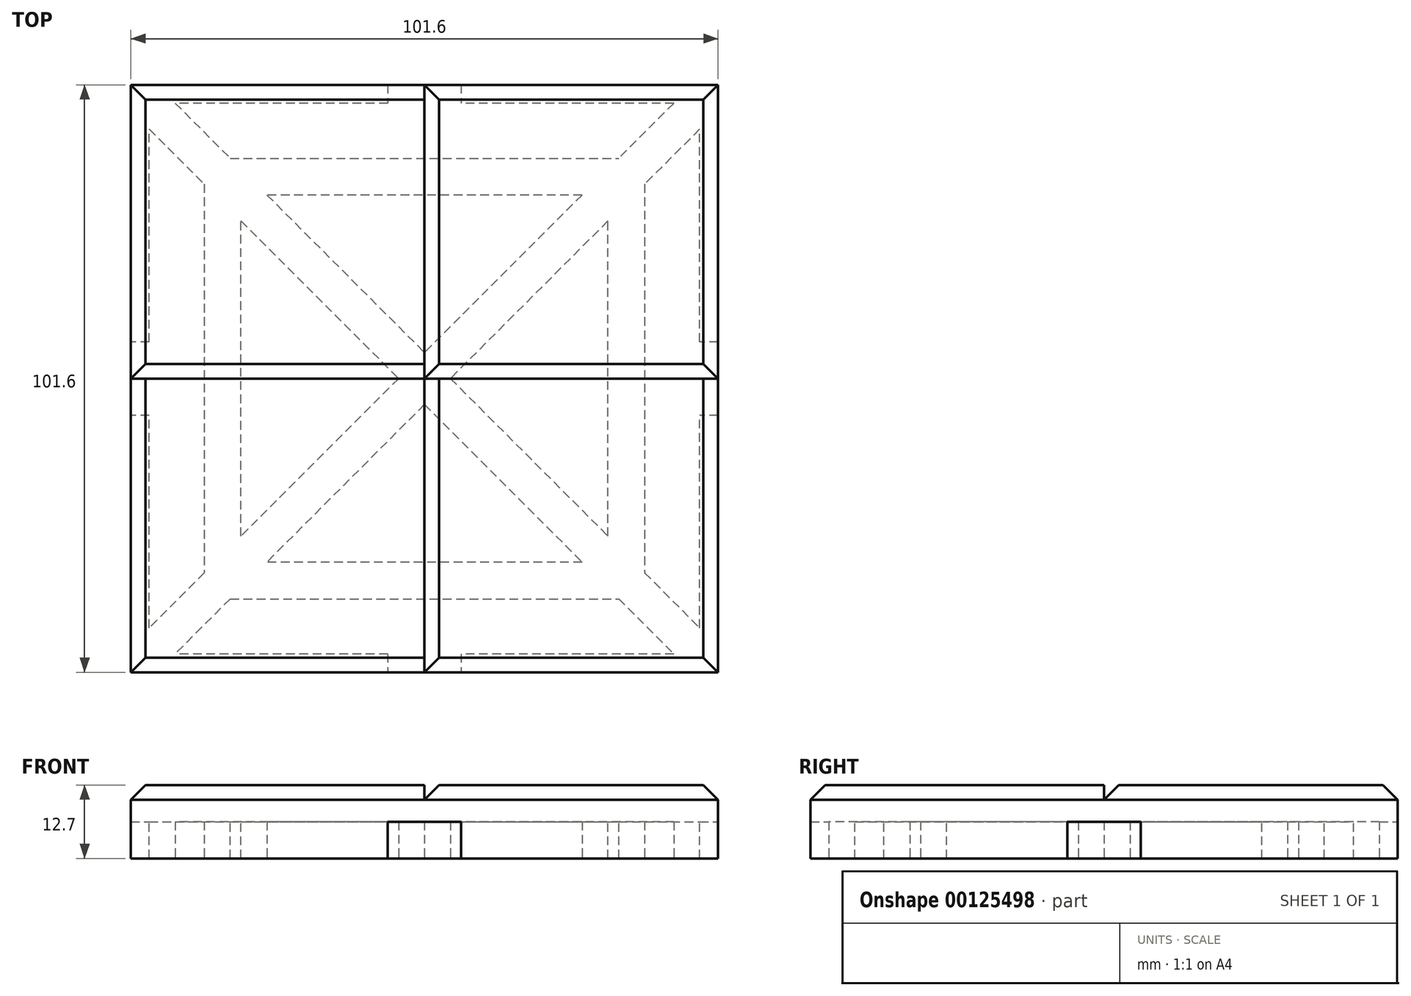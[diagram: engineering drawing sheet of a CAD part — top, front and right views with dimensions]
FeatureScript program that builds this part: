
annotation { "Feature Type Name" : "Feature", "Feature Type Description" : "" }
export const myFeature = defineFeature(function(context is Context, id is Id, definition is map)
    precondition{}
    {
        {
            var Q0;
            Q0=qCreatedBy(makeId("Top.planeOp"),FACE);
            var sketch = newSketch(context, id + "F0", { "sketchPlane" : qUnion([Q0])});
            skLineSegment(sketch, "E0.bottom", {"start": v(50.8, -50.8) * mm, "end": v(-50.8, -50.8) * mm});
            skLineSegment(sketch, "E0.top", {"start": v(50.8, 50.8) * mm, "end": v(-50.8, 50.8) * mm});
            skLineSegment(sketch, "E0.left", {"start": v(50.8, -50.8) * mm, "end": v(50.8, 50.8) * mm});
            skLineSegment(sketch, "E0.right", {"start": v(-50.8, -50.8) * mm, "end": v(-50.8, 50.8) * mm});
            skPoint(sketch, "E0.middle", {"position": v(0, 0) * mm});
            skLineSegment(sketch, "E1.bottom", {"start": v(47.63, -47.62) * mm, "end": v(-47.63, -47.63) * mm});
            skLineSegment(sketch, "E1.top", {"start": v(47.63, 47.63) * mm, "end": v(-47.63, 47.62) * mm});
            skLineSegment(sketch, "E1.left", {"start": v(47.63, -47.62) * mm, "end": v(47.63, 47.63) * mm});
            skLineSegment(sketch, "E1.right", {"start": v(-47.63, -47.63) * mm, "end": v(-47.63, 47.62) * mm});
            skSolve(sketch);
        }
        {
            var Q0;
            Q0=makeQuery(id+"F0.imprint","IMPRINT",FACE,{"disambiguationData":[TD([[makeQuery(id+"F0.imprint","IMPRINT",EDGE,{"derivedFrom":sQuery(id+"F0.wireOp",EDGE,"E0.bottom")}),-1.0]])]});
            var Q1;
            Q1=qNothing();
            var Q2;
            Q2=qNothing();
            extrude(context, id + "F1", {"entities" : qUnion([Q0]), "surfaceEntities" : qUnion([Q1, Q2]), "depth" : 6.35 * mm});
        }
        {
            var Q0;
            Q0=qCreatedBy(makeId("Top.planeOp"),FACE);
            var sketch = newSketch(context, id + "F2", { "sketchPlane" : qUnion([Q0])});
            skLineSegment(sketch, "E2.bottom", {"start": v(50.8, -6.35) * mm, "end": v(-50.8, -6.35) * mm});
            skLineSegment(sketch, "E2.top", {"start": v(50.8, 6.35) * mm, "end": v(-50.8, 6.35) * mm});
            skLineSegment(sketch, "E2.left", {"start": v(50.8, -6.35) * mm, "end": v(50.8, 6.35) * mm});
            skLineSegment(sketch, "E2.right", {"start": v(-50.8, -6.35) * mm, "end": v(-50.8, 6.35) * mm});
            skPoint(sketch, "E2.middle", {"position": v(0, 0) * mm});
            skLineSegment(sketch, "E3.bottom", {"start": v(6.35, 50.8) * mm, "end": v(-6.35, 50.8) * mm});
            skLineSegment(sketch, "E3.top", {"start": v(6.35, -50.8) * mm, "end": v(-6.35, -50.8) * mm});
            skLineSegment(sketch, "E3.left", {"start": v(6.35, 50.8) * mm, "end": v(6.35, -50.8) * mm});
            skLineSegment(sketch, "E3.right", {"start": v(-6.35, 50.8) * mm, "end": v(-6.35, -50.8) * mm});
            skLineSegment(sketch, "E4.bottom", {"start": v(-38.1, 38.1) * mm, "end": v(38.1, 38.1) * mm});
            skLineSegment(sketch, "E4.top", {"start": v(-38.1, -38.1) * mm, "end": v(38.1, -38.1) * mm});
            skLineSegment(sketch, "E4.left", {"start": v(-38.1, 38.1) * mm, "end": v(-38.1, -38.1) * mm});
            skLineSegment(sketch, "E4.right", {"start": v(38.1, 38.1) * mm, "end": v(38.1, -38.1) * mm});
            skLineSegment(sketch, "E5.bottom", {"start": v(31.75, -31.75) * mm, "end": v(-31.75, -31.75) * mm});
            skLineSegment(sketch, "E5.top", {"start": v(31.75, 31.75) * mm, "end": v(-31.75, 31.75) * mm});
            skLineSegment(sketch, "E5.left", {"start": v(31.75, -31.75) * mm, "end": v(31.75, 31.75) * mm});
            skLineSegment(sketch, "E5.right", {"start": v(-31.75, -31.75) * mm, "end": v(-31.75, 31.75) * mm});
            skSolve(sketch);
        }
        {
            var Q0;
            {var subQ0=sQuery(id+"F2.wireOp",EDGE,"E3.bottom");Q0=makeQuery(id+"F2.imprint","IMPRINT",FACE,{"disambiguationData":[TD([[makeQuery(id+"F2.imprint","IMPRINT",EDGE,{"derivedFrom":subQ0}),1.0]])]});}
            var Q1;
            {var subQ0=sQuery(id+"F2.wireOp",EDGE,"E2.left");Q1=makeQuery(id+"F2.imprint","IMPRINT",FACE,{"disambiguationData":[TD([[makeQuery(id+"F2.imprint","IMPRINT",EDGE,{"derivedFrom":subQ0}),1.0]])]});}
            var Q2;
            {var subQ0=sQuery(id+"F2.wireOp",EDGE,"E3.top");Q2=makeQuery(id+"F2.imprint","IMPRINT",FACE,{"disambiguationData":[TD([[makeQuery(id+"F2.imprint","IMPRINT",EDGE,{"derivedFrom":subQ0}),-1.0]])]});}
            var Q3;
            {var subQ0=sQuery(id+"F2.wireOp",EDGE,"E2.right");Q3=makeQuery(id+"F2.imprint","IMPRINT",FACE,{"disambiguationData":[TD([[makeQuery(id+"F2.imprint","IMPRINT",EDGE,{"derivedFrom":subQ0}),-1.0]])]});}
            extrude(context, id + "F3", {"entities" : qUnion([Q0, Q1, Q2, Q3]), "depth" : 25.4 * mm});
        }
        {
            var Q0;
            Q0=makeQuery(id+"F3.opExtrude","SWEPT_BODY",BODY,{"disambiguationData":[OSD([sQuery(id+"F2.wireOp",EDGE,"E3.bottom"),sQuery(id+"F2.wireOp",EDGE,"E3.left"),sQuery(id+"F2.wireOp",EDGE,"E3.right"),sQuery(id+"F2.wireOp",EDGE,"Qsms8eDc-lT19-7mVP-u5gy-GIsI6seksr0S")])]});
            var Q1;
            Q1=makeQuery(id+"F3.opExtrude","SWEPT_BODY",BODY,{"disambiguationData":[OSD([sQuery(id+"F2.wireOp",EDGE,"E2.bottom"),sQuery(id+"F2.wireOp",EDGE,"E2.top"),sQuery(id+"F2.wireOp",EDGE,"E2.left"),sQuery(id+"F2.wireOp",EDGE,"Qsms8eDc-lT19-7mVP-u5gy-GIsI6seksr0S")])]});
            var Q2;
            Q2=makeQuery(id+"F3.opExtrude","SWEPT_BODY",BODY,{"disambiguationData":[OSD([sQuery(id+"F2.wireOp",EDGE,"E3.top"),sQuery(id+"F2.wireOp",EDGE,"E3.left"),sQuery(id+"F2.wireOp",EDGE,"E3.right"),sQuery(id+"F2.wireOp",EDGE,"Qsms8eDc-lT19-7mVP-u5gy-GIsI6seksr0S")])]});
            var Q3;
            Q3=makeQuery(id+"F3.opExtrude","SWEPT_BODY",BODY,{"disambiguationData":[OSD([sQuery(id+"F2.wireOp",EDGE,"E2.bottom"),sQuery(id+"F2.wireOp",EDGE,"E2.top"),sQuery(id+"F2.wireOp",EDGE,"E2.right"),sQuery(id+"F2.wireOp",EDGE,"Qsms8eDc-lT19-7mVP-u5gy-GIsI6seksr0S")])]});
            var Q4;
            Q4=makeQuery(id+"F1.opExtrude","SWEPT_BODY",BODY,{"disambiguationData":[OSD([sQuery(id+"F0.wireOp",EDGE,"E0.bottom"),sQuery(id+"F0.wireOp",EDGE,"E0.top"),sQuery(id+"F0.wireOp",EDGE,"E0.left"),sQuery(id+"F0.wireOp",EDGE,"E0.right"),sQuery(id+"F0.wireOp",EDGE,"E1.bottom"),sQuery(id+"F0.wireOp",EDGE,"E1.top"),sQuery(id+"F0.wireOp",EDGE,"E1.left"),sQuery(id+"F0.wireOp",EDGE,"E1.right")])]});
            booleanBodies(context, id + "F4", {"operationType" : BooleanOperationType.SUBTRACTION, "tools" : qUnion([Q0, Q1, Q2, Q3]), "targets" : qUnion([Q4])});
        }
        {
            var Q0;
            {var subQ0=sQuery(id+"F2.wireOp",EDGE,"E4.left");var subQ3=sQuery(id+"F2.wireOp",EDGE,"E2.bottom");var subQ4=makeQuery(id+"F2.imprint","INTERSECT",VERTEX,{"derivedFrom":[subQ3,subQ0]});Q0=makeQuery(id+"F2.imprint","IMPRINT",FACE,{"disambiguationData":[TD([[makeQuery(id+"F2.imprint","IMPRINT",EDGE,{"disambiguationData":[TD([[subQ4,1.0]])],"derivedFrom":subQ3}),1.0]])]});}
            var Q1;
            {var subQ0=sQuery(id+"F2.wireOp",EDGE,"E4.top");var subQ1=sQuery(id+"F2.wireOp",EDGE,"E3.left");var subQ2=makeQuery(id+"F2.imprint","INTERSECT",VERTEX,{"derivedFrom":[subQ1,subQ0]});Q1=makeQuery(id+"F2.imprint","IMPRINT",FACE,{"disambiguationData":[TD([[makeQuery(id+"F2.imprint","IMPRINT",EDGE,{"disambiguationData":[TD([[subQ2,1.0]])],"derivedFrom":subQ1}),-1.0]])]});}
            var Q2;
            {var subQ0=sQuery(id+"F2.wireOp",EDGE,"E4.right");var subQ3=sQuery(id+"F2.wireOp",EDGE,"E2.bottom");var subQ4=makeQuery(id+"F2.imprint","INTERSECT",VERTEX,{"derivedFrom":[subQ3,subQ0]});Q2=makeQuery(id+"F2.imprint","IMPRINT",FACE,{"disambiguationData":[TD([[makeQuery(id+"F2.imprint","IMPRINT",EDGE,{"disambiguationData":[TD([[subQ4,-1.0]])],"derivedFrom":subQ3}),1.0]])]});}
            var Q3;
            {var subQ0=sQuery(id+"F2.wireOp",EDGE,"E4.right");var subQ1=sQuery(id+"F2.wireOp",EDGE,"E2.bottom");var subQ2=makeQuery(id+"F2.imprint","INTERSECT",VERTEX,{"derivedFrom":[subQ1,subQ0]});Q3=makeQuery(id+"F2.imprint","IMPRINT",FACE,{"disambiguationData":[TD([[makeQuery(id+"F2.imprint","IMPRINT",EDGE,{"disambiguationData":[TD([[subQ2,-1.0]])],"derivedFrom":subQ1}),-1.0]])]});}
            var Q4;
            {var subQ0=sQuery(id+"F2.wireOp",EDGE,"E4.right");var subQ7=sQuery(id+"F2.wireOp",EDGE,"E2.top");var subQ8=makeQuery(id+"F2.imprint","INTERSECT",VERTEX,{"derivedFrom":[subQ7,subQ0]});Q4=makeQuery(id+"F2.imprint","IMPRINT",FACE,{"disambiguationData":[TD([[makeQuery(id+"F2.imprint","IMPRINT",EDGE,{"disambiguationData":[TD([[subQ8,-1.0]])],"derivedFrom":subQ7}),-1.0]])]});}
            var Q5;
            {var subQ0=sQuery(id+"F2.wireOp",EDGE,"E4.bottom");var subQ1=sQuery(id+"F2.wireOp",EDGE,"E3.left");var subQ2=makeQuery(id+"F2.imprint","INTERSECT",VERTEX,{"derivedFrom":[subQ1,subQ0]});Q5=makeQuery(id+"F2.imprint","IMPRINT",FACE,{"disambiguationData":[TD([[makeQuery(id+"F2.imprint","IMPRINT",EDGE,{"disambiguationData":[TD([[subQ2,-1.0]])],"derivedFrom":subQ1}),-1.0]])]});}
            var Q6;
            {var subQ0=sQuery(id+"F2.wireOp",EDGE,"E4.left");var subQ3=sQuery(id+"F2.wireOp",EDGE,"E2.top");var subQ4=makeQuery(id+"F2.imprint","INTERSECT",VERTEX,{"derivedFrom":[subQ3,subQ0]});Q6=makeQuery(id+"F2.imprint","IMPRINT",FACE,{"disambiguationData":[TD([[makeQuery(id+"F2.imprint","IMPRINT",EDGE,{"disambiguationData":[TD([[subQ4,1.0]])],"derivedFrom":subQ3}),-1.0]])]});}
            var Q7;
            {var subQ0=sQuery(id+"F2.wireOp",EDGE,"E4.left");var subQ1=sQuery(id+"F2.wireOp",EDGE,"E2.bottom");var subQ2=makeQuery(id+"F2.imprint","INTERSECT",VERTEX,{"derivedFrom":[subQ1,subQ0]});Q7=makeQuery(id+"F2.imprint","IMPRINT",FACE,{"disambiguationData":[TD([[makeQuery(id+"F2.imprint","IMPRINT",EDGE,{"disambiguationData":[TD([[subQ2,1.0]])],"derivedFrom":subQ1}),-1.0]])]});}
            extrude(context, id + "F5", {"entities" : qUnion([Q0, Q1, Q2, Q3, Q4, Q5, Q6, Q7]), "depth" : 6.35 * mm});
        }
        {
            var Q0;
            Q0=qCreatedBy(makeId("Top.planeOp"),FACE);
            var sketch = newSketch(context, id + "F6", { "sketchPlane" : qUnion([Q0])});
            skLineSegment(sketch, "E6.bottom", {"start": v(3.18, 67.47) * mm, "end": v(-3.17, 67.47) * mm});
            skLineSegment(sketch, "E6.top", {"start": v(3.17, -67.47) * mm, "end": v(-3.18, -67.47) * mm});
            skLineSegment(sketch, "E6.left", {"start": v(3.18, 67.47) * mm, "end": v(3.17, -67.47) * mm});
            skLineSegment(sketch, "E6.right", {"start": v(-3.17, 67.47) * mm, "end": v(-3.18, -67.47) * mm});
            skPoint(sketch, "E6.middle", {"position": v(0, 0) * mm});
            skSolve(sketch);
        }
        {
            var Q0;
            Q0=makeQuery(id+"F6.imprint","IMPRINT",FACE,{"disambiguationData":[TD([[makeQuery(id+"F6.imprint","IMPRINT",EDGE,{"derivedFrom":sQuery(id+"F6.wireOp",EDGE,"E6.bottom")}),1.0]])]});
            extrude(context, id + "F7", {"entities" : qUnion([Q0]), "depth" : 6.35 * mm});
        }
        {
            var Q0;
            Q0=qCreatedBy(makeId("Front.planeOp"),FACE);
            var sketch = newSketch(context, id + "F8", { "sketchPlane" : qUnion([Q0])});
            skLineSegment(sketch, "E7", {"start": v(0, 0) * mm, "end": v(0, 25.4) * mm, "construction": true});
            skSolve(sketch);
        }
        {
            var Q0;
            Q0=makeQuery(id+"F7.opExtrude","SWEPT_BODY",BODY,{"disambiguationData":[OSD([sQuery(id+"F6.wireOp",EDGE,"E6.bottom"),sQuery(id+"F6.wireOp",EDGE,"E6.top"),sQuery(id+"F6.wireOp",EDGE,"E6.left"),sQuery(id+"F6.wireOp",EDGE,"E6.right")])]});
            var Q1;
            Q1=sQuery(id+"F8.wireOp",EDGE,"E7");
            transform(context, id + "F9", {"entities" : qUnion([Q0]), "transformType" : TransformType.ROTATION, "transformAxis" : qUnion([Q1]), "angle" : 45 * degree, "makeCopy" : true});
        }
        {
            var Q0;
            Q0=makeQuery(id+"F7.opExtrude","SWEPT_BODY",BODY,{"disambiguationData":[OSD([sQuery(id+"F6.wireOp",EDGE,"E6.bottom"),sQuery(id+"F6.wireOp",EDGE,"E6.top"),sQuery(id+"F6.wireOp",EDGE,"E6.left"),sQuery(id+"F6.wireOp",EDGE,"E6.right")])]});
            var Q1;
            Q1=sQuery(id+"F8.wireOp",EDGE,"E7");
            transform(context, id + "F10", {"entities" : qUnion([Q0]), "transformType" : TransformType.ROTATION, "transformAxis" : qUnion([Q1]), "angle" : 45 * degree, "oppositeDirection" : true, "makeCopy" : false});
        }
        {
            var Q0;
            Q0=makeQuery(id+"F9.opPattern","COPY",BODY,{"derivedFrom":makeQuery(id+"F7.opExtrude","SWEPT_BODY",BODY,{"disambiguationData":[OSD([sQuery(id+"F6.wireOp",EDGE,"E6.bottom"),sQuery(id+"F6.wireOp",EDGE,"E6.top"),sQuery(id+"F6.wireOp",EDGE,"E6.left"),sQuery(id+"F6.wireOp",EDGE,"E6.right")])]}),"instanceName":"1"});
            var Q1;
            Q1=makeQuery(id+"F4.opBoolean","SPLIT",BODY,{"disambiguationData":[OD(0.0)],"derivedFrom":makeQuery(id+"F1.opExtrude","SWEPT_BODY",BODY,{"disambiguationData":[OSD([sQuery(id+"F0.wireOp",EDGE,"E0.bottom"),sQuery(id+"F0.wireOp",EDGE,"E0.top"),sQuery(id+"F0.wireOp",EDGE,"E0.left"),sQuery(id+"F0.wireOp",EDGE,"E0.right"),sQuery(id+"F0.wireOp",EDGE,"E1.bottom"),sQuery(id+"F0.wireOp",EDGE,"E1.top"),sQuery(id+"F0.wireOp",EDGE,"E1.left"),sQuery(id+"F0.wireOp",EDGE,"E1.right")])]})});
            var Q2;
            Q2=makeQuery(id+"F4.opBoolean","SPLIT",BODY,{"disambiguationData":[OD(2.0)],"derivedFrom":makeQuery(id+"F1.opExtrude","SWEPT_BODY",BODY,{"disambiguationData":[OSD([sQuery(id+"F0.wireOp",EDGE,"E0.bottom"),sQuery(id+"F0.wireOp",EDGE,"E0.top"),sQuery(id+"F0.wireOp",EDGE,"E0.left"),sQuery(id+"F0.wireOp",EDGE,"E0.right"),sQuery(id+"F0.wireOp",EDGE,"E1.bottom"),sQuery(id+"F0.wireOp",EDGE,"E1.top"),sQuery(id+"F0.wireOp",EDGE,"E1.left"),sQuery(id+"F0.wireOp",EDGE,"E1.right")])]})});
            var Q3;
            Q3=makeQuery(id+"F4.opBoolean","SPLIT",BODY,{"disambiguationData":[OD(1.0)],"derivedFrom":makeQuery(id+"F1.opExtrude","SWEPT_BODY",BODY,{"disambiguationData":[OSD([sQuery(id+"F0.wireOp",EDGE,"E0.bottom"),sQuery(id+"F0.wireOp",EDGE,"E0.top"),sQuery(id+"F0.wireOp",EDGE,"E0.left"),sQuery(id+"F0.wireOp",EDGE,"E0.right"),sQuery(id+"F0.wireOp",EDGE,"E1.bottom"),sQuery(id+"F0.wireOp",EDGE,"E1.top"),sQuery(id+"F0.wireOp",EDGE,"E1.left"),sQuery(id+"F0.wireOp",EDGE,"E1.right")])]})});
            var Q4;
            Q4=makeQuery(id+"F4.opBoolean","SPLIT",BODY,{"disambiguationData":[OD(3.0)],"derivedFrom":makeQuery(id+"F1.opExtrude","SWEPT_BODY",BODY,{"disambiguationData":[OSD([sQuery(id+"F0.wireOp",EDGE,"E0.bottom"),sQuery(id+"F0.wireOp",EDGE,"E0.top"),sQuery(id+"F0.wireOp",EDGE,"E0.left"),sQuery(id+"F0.wireOp",EDGE,"E0.right"),sQuery(id+"F0.wireOp",EDGE,"E1.bottom"),sQuery(id+"F0.wireOp",EDGE,"E1.top"),sQuery(id+"F0.wireOp",EDGE,"E1.left"),sQuery(id+"F0.wireOp",EDGE,"E1.right")])]})});
            var Q5;
            Q5=makeQuery(id+"F5.opExtrude","SWEPT_BODY",BODY,{"disambiguationData":[OSD([sQuery(id+"F2.wireOp",EDGE,"E2.bottom"),sQuery(id+"F2.wireOp",EDGE,"E2.top"),sQuery(id+"F2.wireOp",EDGE,"E3.left"),sQuery(id+"F2.wireOp",EDGE,"E3.right"),sQuery(id+"F2.wireOp",EDGE,"E4.bottom"),sQuery(id+"F2.wireOp",EDGE,"E4.top"),sQuery(id+"F2.wireOp",EDGE,"E4.left"),sQuery(id+"F2.wireOp",EDGE,"E4.right"),sQuery(id+"F2.wireOp",EDGE,"E5.bottom"),sQuery(id+"F2.wireOp",EDGE,"E5.top"),sQuery(id+"F2.wireOp",EDGE,"E5.left"),sQuery(id+"F2.wireOp",EDGE,"E5.right")])]});
            var Q6;
            Q6=makeQuery(id+"F7.opExtrude","SWEPT_BODY",BODY,{"disambiguationData":[OSD([sQuery(id+"F6.wireOp",EDGE,"E6.bottom"),sQuery(id+"F6.wireOp",EDGE,"E6.top"),sQuery(id+"F6.wireOp",EDGE,"E6.left"),sQuery(id+"F6.wireOp",EDGE,"E6.right")])]});
            booleanBodies(context, id + "F11", {"operationType" : BooleanOperationType.UNION, "tools" : qUnion([Q0, Q1, Q2, Q3, Q4, Q5, Q6])});
        }
        {
            var Q0;
            {var subQ0=makeQuery(id+"F7.opExtrude","CAP_FACE",FACE,{"disambiguationData":[OSD([sQuery(id+"F6.wireOp",EDGE,"E6.bottom"),sQuery(id+"F6.wireOp",EDGE,"E6.top"),sQuery(id+"F6.wireOp",EDGE,"E6.left"),sQuery(id+"F6.wireOp",EDGE,"E6.right")])],"isStart":false});var subQ1=sQuery(id+"F2.wireOp",EDGE,"E4.right");var subQ2=sQuery(id+"F2.wireOp",EDGE,"E4.left");var subQ3=sQuery(id+"F2.wireOp",EDGE,"E4.top");var subQ4=sQuery(id+"F2.wireOp",EDGE,"E4.bottom");var subQ5=sQuery(id+"F2.wireOp",EDGE,"E3.right");var subQ6=sQuery(id+"F2.wireOp",EDGE,"E3.left");var subQ7=sQuery(id+"F2.wireOp",EDGE,"E2.top");var subQ8=sQuery(id+"F2.wireOp",EDGE,"E2.bottom");var subQ9=sQuery(id+"F0.wireOp",EDGE,"E1.top");var subQ11=sQuery(id+"F0.wireOp",EDGE,"E0.right");var subQ13=sQuery(id+"F0.wireOp",EDGE,"E1.right");var subQ15=sQuery(id+"F0.wireOp",EDGE,"E0.top");var subQ17=sQuery(id+"F2.wireOp",EDGE,"E2.right");var subQ19=sQuery(id+"F0.wireOp",EDGE,"E1.left");var subQ20=sQuery(id+"F0.wireOp",EDGE,"E1.bottom");var subQ21=sQuery(id+"F0.wireOp",EDGE,"E0.left");var subQ22=sQuery(id+"F0.wireOp",EDGE,"E0.bottom");var subQ23=makeQuery(id+"F1.opExtrude","CAP_FACE",FACE,{"disambiguationData":[OSD([subQ22,subQ15,subQ21,subQ11,subQ20,subQ9,subQ19,subQ13])],"isStart":false});var subQ26=sQuery(id+"F2.wireOp",EDGE,"E2.left");Q0=makeQuery(id+"F11.opBoolean","MERGE",FACE,{"derivedFrom":[makeQuery(id+"F4.opBoolean","SPLIT",FACE,{"disambiguationData":[TD([makeQuery(id+"F3.opExtrude","SWEPT_FACE",FACE,{"disambiguationData":[OSD([subQ8]),TDD([makeQuery(id+"F2.imprint","IMPRINT",EDGE,{"disambiguationData":[TD([[makeQuery(id+"F2.imprint","INTERSECT",VERTEX,{"derivedFrom":[subQ8,subQ26]}),-1.0]])],"derivedFrom":subQ8})])]})])],"derivedFrom":subQ23}),makeQuery(id+"F4.opBoolean","SPLIT",FACE,{"disambiguationData":[TD([makeQuery(id+"F3.opExtrude","SWEPT_FACE",FACE,{"disambiguationData":[OSD([subQ8]),TDD([makeQuery(id+"F2.imprint","IMPRINT",EDGE,{"disambiguationData":[TD([[makeQuery(id+"F2.imprint","INTERSECT",VERTEX,{"derivedFrom":[subQ8,subQ17]}),1.0]])],"derivedFrom":subQ8})])]})])],"derivedFrom":subQ23}),makeQuery(id+"F4.opBoolean","SPLIT",FACE,{"disambiguationData":[TD([makeQuery(id+"F3.opExtrude","SWEPT_FACE",FACE,{"disambiguationData":[OSD([subQ7]),TDD([makeQuery(id+"F2.imprint","IMPRINT",EDGE,{"disambiguationData":[TD([[makeQuery(id+"F2.imprint","INTERSECT",VERTEX,{"derivedFrom":[subQ7,subQ26]}),-1.0]])],"derivedFrom":subQ7})])]})])],"derivedFrom":subQ23}),makeQuery(id+"F4.opBoolean","SPLIT",FACE,{"disambiguationData":[TD([makeQuery(id+"F3.opExtrude","SWEPT_FACE",FACE,{"disambiguationData":[OSD([subQ7]),TDD([makeQuery(id+"F2.imprint","IMPRINT",EDGE,{"disambiguationData":[TD([[makeQuery(id+"F2.imprint","INTERSECT",VERTEX,{"derivedFrom":[subQ7,subQ17]}),1.0]])],"derivedFrom":subQ7})])]})])],"derivedFrom":subQ23}),makeQuery(id+"F5.opExtrude","CAP_FACE",FACE,{"disambiguationData":[OSD([subQ8,subQ7,subQ6,subQ5,subQ4,subQ3,subQ2,subQ1,sQuery(id+"F2.wireOp",EDGE,"E5.bottom"),sQuery(id+"F2.wireOp",EDGE,"E5.top"),sQuery(id+"F2.wireOp",EDGE,"E5.left"),sQuery(id+"F2.wireOp",EDGE,"E5.right")])],"isStart":false}),subQ0,makeQuery(id+"F9.opPattern","COPY",FACE,{"derivedFrom":subQ0,"instanceName":"1"})]});}
            var sketch = newSketch(context, id + "F12", { "sketchPlane" : qUnion([Q0])});
            skLineSegment(sketch, "E8.bottom", {"start": v(50.8, 50.8) * mm, "end": v(-50.8, 50.8) * mm});
            skLineSegment(sketch, "E8.top", {"start": v(50.8, -50.8) * mm, "end": v(-50.8, -50.8) * mm});
            skLineSegment(sketch, "E8.left", {"start": v(50.8, 50.8) * mm, "end": v(50.8, -50.8) * mm});
            skLineSegment(sketch, "E8.right", {"start": v(-50.8, 50.8) * mm, "end": v(-50.8, -50.8) * mm});
            skPoint(sketch, "E8.middle", {"position": v(0, 0) * mm});
            skSolve(sketch);
        }
        {
            var Q0;
            Q0=qSketchRegion(id+"F12",true);
            extrude(context, id + "F13", {"entities" : qUnion([Q0]), "operationType" : NewBodyOperationType.ADD, "depth" : 6.35 * mm});
        }
        {
            var Q0;
            Q0=qCreatedBy(makeId("Front.planeOp"),FACE);
            var sketch = newSketch(context, id + "F14", { "sketchPlane" : qUnion([Q0])});
            skLineSegment(sketch, "E9", {"start": v(0, 0) * mm, "end": v(0, 12.7) * mm});
            skLineSegment(sketch, "E10.bottom", {"start": v(0, 12.7) * mm, "end": v(2.54, 12.7) * mm});
            skLineSegment(sketch, "E10.top", {"start": v(0, 10.16) * mm, "end": v(2.54, 10.16) * mm});
            skLineSegment(sketch, "E10.left", {"start": v(0, 12.7) * mm, "end": v(0, 10.16) * mm});
            skLineSegment(sketch, "E10.right", {"start": v(2.54, 12.7) * mm, "end": v(2.54, 10.16) * mm});
            skLineSegment(sketch, "E11.MirrorCS", {"start": v(0, 12.7) * mm, "end": v(-2.54, 12.7) * mm});
            skLineSegment(sketch, "E12.MirrorCS", {"start": v(-2.54, 12.7) * mm, "end": v(-2.54, 10.16) * mm});
            skLineSegment(sketch, "E13.MirrorCS", {"start": v(0, 10.16) * mm, "end": v(-2.54, 10.16) * mm});
            skLineSegment(sketch, "E14", {"start": v(-2.54, 12.7) * mm, "end": v(0, 10.16) * mm});
            skLineSegment(sketch, "E15", {"start": v(2.54, 12.7) * mm, "end": v(0, 10.16) * mm});
            skLineSegment(sketch, "E16", {"start": v(0, 0) * mm, "end": v(-50.8, 0) * mm});
            skLineSegment(sketch, "E17", {"start": v(-50.8, 0) * mm, "end": v(-50.8, 12.7) * mm});
            skLineSegment(sketch, "E18.bottom", {"start": v(-50.8, 12.7) * mm, "end": v(-48.26, 12.7) * mm});
            skLineSegment(sketch, "E18.top", {"start": v(-50.8, 10.16) * mm, "end": v(-48.26, 10.16) * mm});
            skLineSegment(sketch, "E18.left", {"start": v(-50.8, 12.7) * mm, "end": v(-50.8, 10.16) * mm});
            skLineSegment(sketch, "E18.right", {"start": v(-48.26, 12.7) * mm, "end": v(-48.26, 10.16) * mm});
            skLineSegment(sketch, "E19", {"start": v(-48.26, 12.7) * mm, "end": v(-50.8, 10.16) * mm});
            skLineSegment(sketch, "E20.MirrorCS", {"start": v(0, 0) * mm, "end": v(50.8, 0) * mm});
            skLineSegment(sketch, "E21.MirrorCS", {"start": v(50.8, 0) * mm, "end": v(50.8, 12.7) * mm});
            skLineSegment(sketch, "E22.MirrorCS", {"start": v(50.8, 12.7) * mm, "end": v(48.26, 12.7) * mm});
            skLineSegment(sketch, "E23.MirrorCS", {"start": v(48.26, 12.7) * mm, "end": v(50.8, 10.16) * mm});
            skLineSegment(sketch, "E24.MirrorCS", {"start": v(50.8, 10.16) * mm, "end": v(48.26, 10.16) * mm});
            skLineSegment(sketch, "E25.MirrorCS", {"start": v(48.26, 12.7) * mm, "end": v(48.26, 10.16) * mm});
            skSolve(sketch);
        }
        {
            var Q0;
            Q0=makeQuery(id+"F14.imprint","IMPRINT",FACE,{"disambiguationData":[TD([[makeQuery(id+"F14.imprint","IMPRINT",EDGE,{"derivedFrom":sQuery(id+"F14.wireOp",EDGE,"E10.left")}),-1.0]])]});
            var Q1;
            Q1=makeQuery(id+"F14.imprint","IMPRINT",FACE,{"disambiguationData":[TD([[makeQuery(id+"F14.imprint","IMPRINT",EDGE,{"derivedFrom":sQuery(id+"F14.wireOp",EDGE,"E10.bottom")}),-1.0]])]});
            extrude(context, id + "F15", {"entities" : qUnion([Q0, Q1]), "endBound" : BoundingType.SYMMETRIC, "oppositeDirection" : true, "depth" : 152.4 * mm});
        }
        {
            var Q0;
            Q0=makeQuery(id+"F15.opExtrude","SWEPT_BODY",BODY,{"disambiguationData":[OSD([sQuery(id+"F14.wireOp",EDGE,"E10.bottom"),sQuery(id+"F14.wireOp",EDGE,"E11.MirrorCS"),sQuery(id+"F14.wireOp",EDGE,"E14"),sQuery(id+"F14.wireOp",EDGE,"E15")])]});
            var Q1;
            Q1=sQuery(id+"F8.wireOp",EDGE,"E7");
            transform(context, id + "F16", {"entities" : qUnion([Q0]), "transformType" : TransformType.ROTATION, "transformAxis" : qUnion([Q1]), "angle" : 90 * degree, "makeCopy" : true});
        }
        {
            var Q0;
            Q0=makeQuery(id+"F16.opPattern","COPY",BODY,{"derivedFrom":makeQuery(id+"F15.opExtrude","SWEPT_BODY",BODY,{"disambiguationData":[OSD([sQuery(id+"F14.wireOp",EDGE,"E10.bottom"),sQuery(id+"F14.wireOp",EDGE,"E11.MirrorCS"),sQuery(id+"F14.wireOp",EDGE,"E14"),sQuery(id+"F14.wireOp",EDGE,"E15")])]}),"instanceName":"1"});
            var Q1;
            Q1=makeQuery(id+"F15.opExtrude","SWEPT_BODY",BODY,{"disambiguationData":[OSD([sQuery(id+"F14.wireOp",EDGE,"E10.bottom"),sQuery(id+"F14.wireOp",EDGE,"E11.MirrorCS"),sQuery(id+"F14.wireOp",EDGE,"E14"),sQuery(id+"F14.wireOp",EDGE,"E15")])]});
            var Q2;
            Q2=makeQuery(id+"F9.opPattern","COPY",BODY,{"derivedFrom":makeQuery(id+"F7.opExtrude","SWEPT_BODY",BODY,{"disambiguationData":[OSD([sQuery(id+"F6.wireOp",EDGE,"E6.bottom"),sQuery(id+"F6.wireOp",EDGE,"E6.top"),sQuery(id+"F6.wireOp",EDGE,"E6.left"),sQuery(id+"F6.wireOp",EDGE,"E6.right")])]}),"instanceName":"1"});
            booleanBodies(context, id + "F17", {"operationType" : BooleanOperationType.SUBTRACTION, "tools" : qUnion([Q0, Q1]), "targets" : qUnion([Q2])});
        }
        {
            var Q0;
            Q0=makeQuery(id+"F14.imprint","IMPRINT",FACE,{"disambiguationData":[TD([[makeQuery(id+"F14.imprint","IMPRINT",EDGE,{"derivedFrom":sQuery(id+"F14.wireOp",EDGE,"E18.bottom")}),-1.0]])]});
            var Q1;
            {var subQ0=sQuery(id+"F14.wireOp",EDGE,"E22.MirrorCS");Q1=makeQuery(id+"F14.imprint","IMPRINT",FACE,{"disambiguationData":[TD([[makeQuery(id+"F14.imprint","IMPRINT",EDGE,{"derivedFrom":subQ0}),1.0]])]});}
            extrude(context, id + "F18", {"entities" : qUnion([Q0, Q1]), "endBound" : BoundingType.SYMMETRIC, "depth" : 152.4 * mm});
        }
        {
            var Q0;
            Q0=makeQuery(id+"F18.opExtrude","SWEPT_BODY",BODY,{"disambiguationData":[OSD([sQuery(id+"F14.wireOp",EDGE,"E18.bottom"),sQuery(id+"F14.wireOp",EDGE,"E18.left"),sQuery(id+"F14.wireOp",EDGE,"E19")])]});
            var Q1;
            Q1=makeQuery(id+"F18.opExtrude","SWEPT_BODY",BODY,{"disambiguationData":[OSD([sQuery(id+"F14.wireOp",EDGE,"E21.MirrorCS"),sQuery(id+"F14.wireOp",EDGE,"E22.MirrorCS"),sQuery(id+"F14.wireOp",EDGE,"E23.MirrorCS")])]});
            var Q2;
            Q2=sQuery(id+"F8.wireOp",EDGE,"E7");
            transform(context, id + "F19", {"entities" : qUnion([Q0, Q1]), "transformType" : TransformType.ROTATION, "transformAxis" : qUnion([Q2]), "angle" : 90 * degree, "makeCopy" : true});
        }
        {
            var Q0;
            Q0=makeQuery(id+"F19.opPattern","COPY",BODY,{"derivedFrom":makeQuery(id+"F18.opExtrude","SWEPT_BODY",BODY,{"disambiguationData":[OSD([sQuery(id+"F14.wireOp",EDGE,"E21.MirrorCS"),sQuery(id+"F14.wireOp",EDGE,"E22.MirrorCS"),sQuery(id+"F14.wireOp",EDGE,"E23.MirrorCS")])]}),"instanceName":"1"});
            var Q1;
            Q1=makeQuery(id+"F18.opExtrude","SWEPT_BODY",BODY,{"disambiguationData":[OSD([sQuery(id+"F14.wireOp",EDGE,"E18.bottom"),sQuery(id+"F14.wireOp",EDGE,"E18.left"),sQuery(id+"F14.wireOp",EDGE,"E19")])]});
            var Q2;
            Q2=makeQuery(id+"F18.opExtrude","SWEPT_BODY",BODY,{"disambiguationData":[OSD([sQuery(id+"F14.wireOp",EDGE,"E21.MirrorCS"),sQuery(id+"F14.wireOp",EDGE,"E22.MirrorCS"),sQuery(id+"F14.wireOp",EDGE,"E23.MirrorCS")])]});
            var Q3;
            Q3=makeQuery(id+"F19.opPattern","COPY",BODY,{"derivedFrom":makeQuery(id+"F18.opExtrude","SWEPT_BODY",BODY,{"disambiguationData":[OSD([sQuery(id+"F14.wireOp",EDGE,"E18.bottom"),sQuery(id+"F14.wireOp",EDGE,"E18.left"),sQuery(id+"F14.wireOp",EDGE,"E19")])]}),"instanceName":"1"});
            var Q4;
            Q4=makeQuery(id+"F9.opPattern","COPY",BODY,{"derivedFrom":makeQuery(id+"F7.opExtrude","SWEPT_BODY",BODY,{"disambiguationData":[OSD([sQuery(id+"F6.wireOp",EDGE,"E6.bottom"),sQuery(id+"F6.wireOp",EDGE,"E6.top"),sQuery(id+"F6.wireOp",EDGE,"E6.left"),sQuery(id+"F6.wireOp",EDGE,"E6.right")])]}),"instanceName":"1"});
            booleanBodies(context, id + "F20", {"operationType" : BooleanOperationType.SUBTRACTION, "tools" : qUnion([Q0, Q1, Q2, Q3]), "targets" : qUnion([Q4])});
        }
    });
